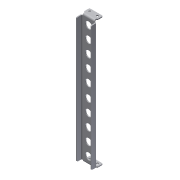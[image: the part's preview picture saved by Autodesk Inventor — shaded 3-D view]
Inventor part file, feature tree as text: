
AUTODESK INVENTOR PART (.ipt)
format: ipt  version: 2013 (Build 170138000, 138)  size: 266,240 bytes
history: native  units: in
note: dims shown in document units (in); Inventor stores cm internally (conversion verified against a paired STEP export)
features: reference x8, sheet_metal_op x7, sketch x5, other x5, hole x1, fillet x1, pattern_linear x1, mirror x1
ambient origin geometry x8: Origin, YZ Plane, XZ Plane, XY Plane, X Axis, Y Axis, Z Axis, Center Point
bodies: Solid1 (feature_tree)
feature tree (29):
  sheet_metal_op  "Face1"
  sheet_metal_op  "Flange1"
  hole  "Hole1"  [1 undecoded]
  sheet_metal_op  "Flange2"
  fillet  "Fillet1"  Radius=0.125in
  pattern_linear  "Rectangular Pattern1"  Spacing1=1.0in  [1 undecoded]
  mirror  "Mirror1"
  sketch  "Sketch1"  dims[d0=0.25in d1=0.25in d2=0.125in]
  reference  "Reference1"
  reference  "Reference2"
  reference  "Reference3"
  reference  "Reference4"
  reference  "Reference5"
  reference  "Reference6"
  other  "Plate1"
  sketch  "Sketch2"  dims[d3=0.125in]
  other  "Plate2"
  sheet_metal_op  "Bend1"
  sheet_metal_op  "Corner1"
  sketch  "Sketch3"  dims[d4=0.0625in]
  reference  "Reference7"
  reference  "Reference8"
  sketch  "Sketch4"  dims[d5=0.25in]
  other  "Plate3"
  sheet_metal_op  "Bend2"
  sheet_metal_op  "Corner2"
  sketch  "Sketch5"  dims[d6=0.125in d7=1.0in d8=90.0deg d9=0.125in d10=0.5in d11=0.125in d12=0.125in d13=0.38in d14=0.38in d16=0.4in d17=0.26in d18=0.75in d19=0.375in d20=0.25in d21=0.5635in d22=0.125in d23=0.8108in d24=0.125in d25=0.0625in d26=0.25in d27=0.125in d28=0.75in d29=90.0deg d30=0.125in d31=0.5in d32=0.125in d33=0.125in d34=0.125in d35=0.875in d38=0.75in d39=0.875in d40=0.0in d41=1.9685in d43=1.625in]
  other  "Cut1"
  other  "Definition1"
note: 2 required parameter values undecoded (feature->parameter linkage not recoverable at this tier; creation-order binding heuristic only, values carry confidence <= 0.55)
